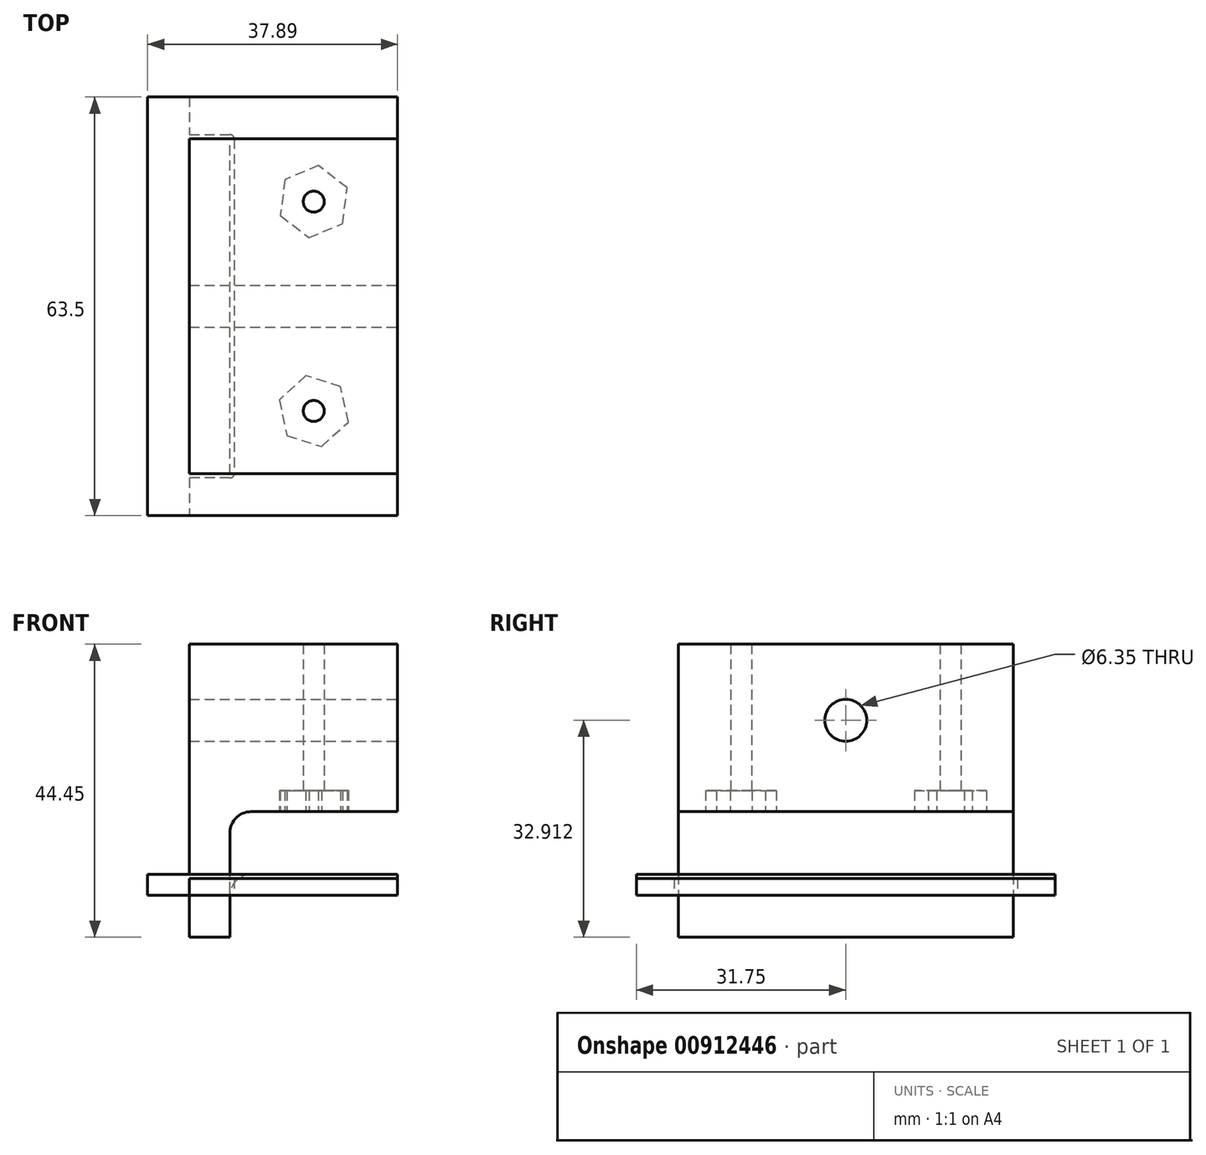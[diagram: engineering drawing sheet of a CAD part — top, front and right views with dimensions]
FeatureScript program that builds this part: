
annotation { "Feature Type Name" : "Feature", "Feature Type Description" : "" }
export const myFeature = defineFeature(function(context is Context, id is Id, definition is map)
    precondition{}
    {
        {
            var Q0;
            Q0=qCreatedBy(makeId("Front.planeOp"),FACE);
            var sketch = newSketch(context, id + "F0", { "sketchPlane" : qUnion([Q0])});
            skLineSegment(sketch, "E0", {"start": v(-4.4, 0) * mm, "end": v(17.83, 0) * mm});
            skLineSegment(sketch, "E1", {"start": v(17.83, 0) * mm, "end": v(17.83, 25.4) * mm});
            skLineSegment(sketch, "E2", {"start": v(17.83, 25.4) * mm, "end": v(-13.71, 25.4) * mm});
            skLineSegment(sketch, "E3", {"start": v(-13.71, 25.4) * mm, "end": v(-13.71, -19.05) * mm});
            skLineSegment(sketch, "E4", {"start": v(-13.71, -19.05) * mm, "end": v(-7.57, -19.05) * mm});
            skLineSegment(sketch, "E5", {"start": v(-7.57, -19.05) * mm, "end": v(-7.57, -3.18) * mm});
            skPoint(sketch, "E6.visualSharp", {"position": v(-7.57, 0) * mm});
            skArc(sketch, "E6.filletArc", {"start": v(-4.4, 0) * mm, "mid": v(-6.64, -0.93) * mm, "end": v(-7.57, -3.18) * mm});
            skSolve(sketch);
        }
        {
            var Q0;
            Q0=makeQuery(id+"F0.imprint","IMPRINT",FACE,{"disambiguationData":[TD([[makeQuery(id+"F0.imprint","IMPRINT",EDGE,{"derivedFrom":sQuery(id+"F0.wireOp",EDGE,"E0")}),1.0]])]});
            extrude(context, id + "F1", {"entities" : qUnion([Q0]), "endBound" : BoundingType.SYMMETRIC, "depth" : 50.8 * mm, "offsetDistance" : 25.4 * mm});
        }
        {
            var Q0;
            Q0=makeQuery(id+"F1.opExtrude","SWEPT_FACE",FACE,{"disambiguationData":[OSD([sQuery(id+"F0.wireOp",EDGE,"E1")])]});
            var sketch = newSketch(context, id + "F2", { "sketchPlane" : qUnion([Q0])});
            skPoint(sketch, "E7", {"position": v(0, 13.86) * mm});
            skSolve(sketch);
        }
        {
            var Q0;
            Q0=sQuery(id+"F2.wireOp",VERTEX,"E7");
            var Q1;
            Q1=makeQuery(id+"F1.opExtrude","SWEPT_BODY",BODY,{"disambiguationData":[OSD([sQuery(id+"F0.wireOp",EDGE,"E0"),sQuery(id+"F0.wireOp",EDGE,"E1"),sQuery(id+"F0.wireOp",EDGE,"E2"),sQuery(id+"F0.wireOp",EDGE,"E3"),sQuery(id+"F0.wireOp",EDGE,"E4"),sQuery(id+"F0.wireOp",EDGE,"E5"),sQuery(id+"F0.wireOp",EDGE,"E6.filletArc")])]});
            hole(context, id + "F3", {"style" : HoleStyle.SIMPLE, "endStyle" : HoleEndStyle.THROUGH, "holeDiameter" : 6.35 * mm, "majorDiameter" : 6.35 * mm, "isTappedThrough" : true, "tappedDepth" : 12.7 * mm, "tapClearance" : 3, "locations" : qUnion([Q0]), "scope" : qUnion([Q1])});
        }
        {
            var Q0;
            Q0=makeQuery(id+"F1.opExtrude","SWEPT_FACE",FACE,{"disambiguationData":[OSD([sQuery(id+"F0.wireOp",EDGE,"E0")])]});
            var sketch = newSketch(context, id + "F4", { "sketchPlane" : qUnion([Q0])});
            skPoint(sketch, "E8", {"position": v(5.13, 15.88) * mm});
            skPoint(sketch, "E9", {"position": v(5.13, -15.88) * mm});
            skSolve(sketch);
        }
        {
            var Q0;
            {var subQ0=sQuery(id+"F0.wireOp",EDGE,"E0");Q0=makeQuery(id+"F4.imprint","IMPRINT",FACE,{"disambiguationData":[TD([[makeQuery(id+"F4.imprint","IMPRINT",EDGE,{"derivedFrom":makeQuery(id+"F1.opExtrude","CAP_EDGE",EDGE,{"disambiguationData":[OSD([subQ0])],"isStart":true})}),1.0]])]});}
            var sketch = newSketch(context, id + "F5", { "sketchPlane" : qUnion([Q0])});
            skCircle(sketch, "E10.cCircle", {"center": v(5.13, -15.88) * mm, "radius": 4.76 * mm, "construction": true});
            skLineSegment(sketch, "E10.0", {"start": v(5.85, -21.33) * mm, "end": v(0.77, -19.22) * mm});
            skLineSegment(sketch, "E10.1", {"start": v(0.77, -19.22) * mm, "end": v(0.05, -13.77) * mm});
            skLineSegment(sketch, "E10.2", {"start": v(0.05, -13.77) * mm, "end": v(4.41, -10.42) * mm});
            skLineSegment(sketch, "E10.3", {"start": v(4.41, -10.42) * mm, "end": v(9.5, -12.53) * mm});
            skLineSegment(sketch, "E10.4", {"start": v(9.5, -12.53) * mm, "end": v(10.2, -17.98) * mm});
            skLineSegment(sketch, "E10.5", {"start": v(10.2, -17.98) * mm, "end": v(5.85, -21.33) * mm});
            skPoint(sketch, "E10.0.midPoint", {"position": v(3.3, -20.28) * mm});
            skCircle(sketch, "E11.cCircle", {"center": v(5.13, 15.88) * mm, "radius": 4.76 * mm, "construction": true});
            skLineSegment(sketch, "E11.0", {"start": v(9.2, 12.17) * mm, "end": v(3.95, 10.5) * mm});
            skLineSegment(sketch, "E11.1", {"start": v(3.95, 10.5) * mm, "end": v(-0.11, 14.2) * mm});
            skLineSegment(sketch, "E11.2", {"start": v(-0.11, 14.2) * mm, "end": v(1.07, 19.58) * mm});
            skLineSegment(sketch, "E11.3", {"start": v(1.07, 19.58) * mm, "end": v(6.3, 21.25) * mm});
            skLineSegment(sketch, "E11.4", {"start": v(6.3, 21.25) * mm, "end": v(10.37, 17.54) * mm});
            skLineSegment(sketch, "E11.5", {"start": v(10.37, 17.54) * mm, "end": v(9.2, 12.17) * mm});
            skPoint(sketch, "E11.0.midPoint", {"position": v(6.57, 11.34) * mm});
            skSolve(sketch);
        }
        {
            var Q0;
            Q0=makeQuery(id+"F5.imprint","IMPRINT",FACE,{"disambiguationData":[TD([[makeQuery(id+"F5.imprint","IMPRINT",EDGE,{"derivedFrom":sQuery(id+"F5.wireOp",EDGE,"E11.0")}),-1.0]])]});
            var Q1;
            Q1=makeQuery(id+"F5.imprint","IMPRINT",FACE,{"disambiguationData":[TD([[makeQuery(id+"F5.imprint","IMPRINT",EDGE,{"derivedFrom":sQuery(id+"F5.wireOp",EDGE,"E10.0")}),-1.0]])]});
            extrude(context, id + "F6", {"entities" : qUnion([Q0, Q1]), "operationType" : NewBodyOperationType.REMOVE, "oppositeDirection" : true, "depth" : 3.17 * mm, "offsetDistance" : 25.4 * mm});
        }
        {
            var Q0;
            Q0=sQuery(id+"F4.wireOp",VERTEX,"E9");
            var Q1;
            Q1=sQuery(id+"F4.wireOp",VERTEX,"E8");
            var Q2;
            Q2=makeQuery(id+"F1.opExtrude","SWEPT_BODY",BODY,{"disambiguationData":[OSD([sQuery(id+"F0.wireOp",EDGE,"E0"),sQuery(id+"F0.wireOp",EDGE,"E1"),sQuery(id+"F0.wireOp",EDGE,"E2"),sQuery(id+"F0.wireOp",EDGE,"E3"),sQuery(id+"F0.wireOp",EDGE,"E4"),sQuery(id+"F0.wireOp",EDGE,"E5"),sQuery(id+"F0.wireOp",EDGE,"E6.filletArc")])]});
            hole(context, id + "F7", {"style" : HoleStyle.SIMPLE, "endStyle" : HoleEndStyle.THROUGH, "holeDiameter" : 3.17 * mm, "majorDiameter" : 6.35 * mm, "isTappedThrough" : true, "tappedDepth" : 12.7 * mm, "tapClearance" : 3, "locations" : qUnion([Q0, Q1]), "scope" : qUnion([Q2])});
        }
        {
            var Q0;
            Q0=qCreatedBy(makeId("Top.planeOp"),FACE);
            cPlane(context, id + "F8", {"entities" : qUnion([Q0]), "cplaneType" : CPlaneType.OFFSET, "offset" : 12.7 * mm, "oppositeDirection" : true, "width" : 152.4 * mm, "height" : 152.4 * mm});
        }
        {
            var Q0;
            Q0=qCreatedBy(id+"F8.planeOp",FACE);
            var sketch = newSketch(context, id + "F9", { "sketchPlane" : qUnion([Q0])});
            skLineSegment(sketch, "E12", {"start": v(17.83, 31.75) * mm, "end": v(-13.71, 31.75) * mm});
            skLineSegment(sketch, "E13", {"start": v(-13.71, 31.75) * mm, "end": v(-13.71, 25.4) * mm});
            skLineSegment(sketch, "E14", {"start": v(-13.71, 25.4) * mm, "end": v(-7.57, 25.4) * mm});
            skLineSegment(sketch, "E15", {"start": v(-7.57, 25.4) * mm, "end": v(-7.57, -25.4) * mm});
            skLineSegment(sketch, "E16", {"start": v(-7.57, -25.4) * mm, "end": v(-13.71, -25.4) * mm});
            skLineSegment(sketch, "E17", {"start": v(-13.71, -25.4) * mm, "end": v(-13.71, -31.75) * mm});
            skLineSegment(sketch, "E18", {"start": v(-13.71, -31.75) * mm, "end": v(17.83, -31.75) * mm});
            skLineSegment(sketch, "E19", {"start": v(17.83, -31.75) * mm, "end": v(17.83, 31.75) * mm});
            skLineSegment(sketch, "E20.0", {"start": v(-7.57, -26.04) * mm, "end": v(-13.71, -26.04) * mm});
            skLineSegment(sketch, "E20.1", {"start": v(-6.94, 25.4) * mm, "end": v(-6.94, -25.4) * mm});
            skLineSegment(sketch, "E20.2", {"start": v(-13.71, 26.04) * mm, "end": v(-7.57, 26.04) * mm});
            skPoint(sketch, "E21.visualSharp", {"position": v(-6.94, -26.04) * mm});
            skArc(sketch, "E21.filletArc", {"start": v(-7.57, -26.04) * mm, "mid": v(-7.12, -25.85) * mm, "end": v(-6.94, -25.4) * mm});
            skPoint(sketch, "E22.visualSharp", {"position": v(-6.94, 26.04) * mm});
            skArc(sketch, "E22.filletArc", {"start": v(-6.94, 25.4) * mm, "mid": v(-7.12, 25.85) * mm, "end": v(-7.57, 26.04) * mm});
            skSolve(sketch);
        }
        {
            var Q0;
            {var subQ4=sQuery(id+"F9.wireOp",EDGE,"E12");Q0=makeQuery(id+"F9.imprint","IMPRINT",FACE,{"disambiguationData":[TD([[makeQuery(id+"F9.imprint","IMPRINT",EDGE,{"derivedFrom":subQ4}),1.0]])]});}
            extrude(context, id + "F10", {"entities" : qUnion([Q0]), "depth" : 2.54 * mm, "offsetDistance" : 25.4 * mm});
        }
        {
            var Q0;
            Q0=qCreatedBy(id+"F8.planeOp",FACE);
            var sketch = newSketch(context, id + "F11", { "sketchPlane" : qUnion([Q0])});
            skLineSegment(sketch, "E23.bottom", {"start": v(17.83, -31.75) * mm, "end": v(-20.06, -31.75) * mm});
            skLineSegment(sketch, "E23.top", {"start": v(17.83, 31.75) * mm, "end": v(-20.06, 31.75) * mm});
            skLineSegment(sketch, "E23.left", {"start": v(17.83, -31.75) * mm, "end": v(17.83, 31.75) * mm});
            skLineSegment(sketch, "E23.right", {"start": v(-20.06, -31.75) * mm, "end": v(-20.06, 31.75) * mm});
            skLineSegment(sketch, "E24.bottom", {"start": v(-7.57, -25.4) * mm, "end": v(-13.71, -25.4) * mm});
            skLineSegment(sketch, "E24.top", {"start": v(-4.4, 25.4) * mm, "end": v(-13.71, 25.4) * mm});
            skLineSegment(sketch, "E24.left", {"start": v(-7.57, -25.4) * mm, "end": v(-7.57, 25.4) * mm});
            skLineSegment(sketch, "E24.right", {"start": v(-13.71, -25.4) * mm, "end": v(-13.71, 25.4) * mm});
            skSolve(sketch);
        }
        {
            var Q0;
            Q0=makeQuery(id+"F11.imprint","IMPRINT",FACE,{"disambiguationData":[TD([[makeQuery(id+"F11.imprint","IMPRINT",EDGE,{"derivedFrom":sQuery(id+"F11.wireOp",EDGE,"E23.bottom")}),-1.0]])]});
            extrude(context, id + "F12", {"entities" : qUnion([Q0]), "depth" : 3.17 * mm, "offsetDistance" : 25.4 * mm});
        }
        {
            var Q0;
            Q0=makeQuery(id+"F12.opExtrude","CAP_EDGE",EDGE,{"disambiguationData":[OSD([sQuery(id+"F11.wireOp",EDGE,"E24.left")])],"isStart":false});
            fillet(context, id + "F13", {"entities" : qUnion([Q0]), "radius" : 3.17 * mm, "tangentPropagation" : true, "allowEdgeOverflow" : false});
        }
    });
